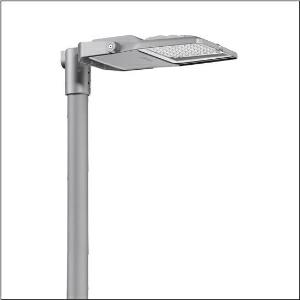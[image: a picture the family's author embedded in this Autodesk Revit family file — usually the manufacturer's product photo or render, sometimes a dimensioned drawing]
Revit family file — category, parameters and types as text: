
# Revit family: floodlight_fl_21_mini___pl61_5xa7776d2c3a_4c8f
name_source: partatom
category: Lighting Fixtures
units: mm (PartAtom-declared; Revit-internal decimal feet)

## family parameters
Cut with Voids When Loaded = No
Host = Face
Light Source = No
Part Type = Normal
Room Calculation Point = No
Round Connector Dimension = Use Diameter
Shared = No

## types (1)
- --- (1 x LED, 17510 lm, 142.9 W, 3000K)
    Apparent Load = 143 VA
    CIE Flux Codes = 33 65 98 100 100
    Color Rendering = 70
    Color Temperature = 3000K
    Default Elevation = 1800 mm
    Description = Floodlight FL 21 mini, floodlight, primary light control with lens, of PMMA, primary optical cover: protective disc, of toughened safety glass, transparent, light distribution: PL61, light emission: direct distribution, installation type: surface-mounted, LED, High Power LED, rated luminous flux: 17.510lm, luminous efficacy: 123lm/W, light colour: 730, colour temperature: 3000K, control: flexible luminous flux parameterisation, time-dependent luminous flux control, constant luminous flux control, overheat protection, presetting dimming logarithmic, with terminal, 6-pole, mains connection: 220..240V, AC, 50/60Hz, start of lifetime: 143W, end of service life: 151W, reduction: 63W, luminaire housing, of diecast aluminium, powder-coated, Siteco® metallic grey (DB 702S), corrosivity category C5 mid according to DIN EN ISO 12944, sealing non-destructively replaceable, please order mast flange separately, mast bracket, of steel, galvanised, powder-coated, Siteco® metallic grey (DB 702S), Smart Interface below and above, protection rating (complete): IP66, insulation class (complete): insulation class II (safety insulation), certification: CE, ENEC, VDE, protection symbol: D, impact resistance: IK08, permissible operating ambient temperature: -40..+40°C, permissible operating ambient temperature for outdoor applications: -40..+50°C, standard: DIN EN 12944, LABS conformity tested according to VDMA 24364:2018-05, packaging unit: 1 piece

Light Distribution: PL61
    Height = 70 mm
    Lamp = 1 x LED
    Lamp Light Flux = 17510 lm
    Lamp Power = 142.9 W
    Lamp count = 1
    Length = 485 mm
    Luminous efficacy = 123 lm/W
    Manufacturer = Siteco
    ModVariant = No
    Model = 5XA7776D2C3A
    Number of Poles = 1
    OnlyDefault = Yes
    Power Factor = 1
    Product Name = Floodlight FL 21 mini | PL61
    Product group = floodlight | pylon annexe
    ProductGroupID = 6200
    Protection Class = Protection class II
    Protection Degree = IP 66
    RLX_Detail_Level = 1
    RLX_Emergency_Light_Flux = 0 lm
    RLX_Emergency_Type = 0
    RLX_Emergency_Type_DB = No
    RlxData = <blob elided: 101245 chars, md5=f2603936>
    Socket = socket
    Standby Power = 0 W
    System Light Flux = 17510 lm
    System Power = 143 W
    Type Comments = factory setting: luminous flux: 100 % | dim-lin: 254 | 730 mA
    Type Image = l_1007125.jpg
    URL = http://relux.com
    VarID = @adj_104929
    Voltage = 0 V
    Weight = 0.00 kg
    Width = 337 mm

## geometry (parser evidence)
native form markers: Blend x4, Sweep x10
no freeform markers — native parametric forms only
